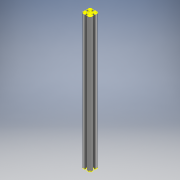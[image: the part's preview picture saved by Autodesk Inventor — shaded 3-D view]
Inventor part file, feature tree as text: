
AUTODESK INVENTOR PART (.ipt)
format: ipt  version: 2018.3 (Build 223284000, 284)  size: 726,016 bytes
history: native  units: mm
features: sketch x5, projected_geometry x5, extrude x3, plane x1, fillet x1
ambient origin geometry x8: Origin, YZ Plane, XZ Plane, XY Plane, X Axis, Y Axis, Z Axis, Center Point
bodies: Solid1 (feature_tree)
feature tree (15):
  sketch  "Sketch1"  dims[d0=10.0mm d1=0.0mm d2=165.1mm d3=0.0mm]
  plane  "Work Plane1"
  extrude  "Extrusion1"  Depth=165.1mm TaperAngle=0.0deg
  sketch  "Sketch2"  dims[d4=29.4mm d5=0.0mm]
  extrude  "Extrusion2"  [1 undecoded]
  extrude  "Extrusion3"  [1 undecoded]
  sketch  "Sketch5"
  projected_geometry  "Projected Loop1"
  projected_geometry  "Projected Loop2"
  sketch  "Sketch3"
  projected_geometry  "Projected Loop3"
  sketch  "Sketch4"
  projected_geometry  "Projected Loop4"
  projected_geometry  "Projected Loop5"
  fillet  "Fillet6"  [1 undecoded]
note: 3 required parameter values undecoded (feature->parameter linkage not recoverable at this tier; creation-order binding heuristic only, values carry confidence <= 0.55)
